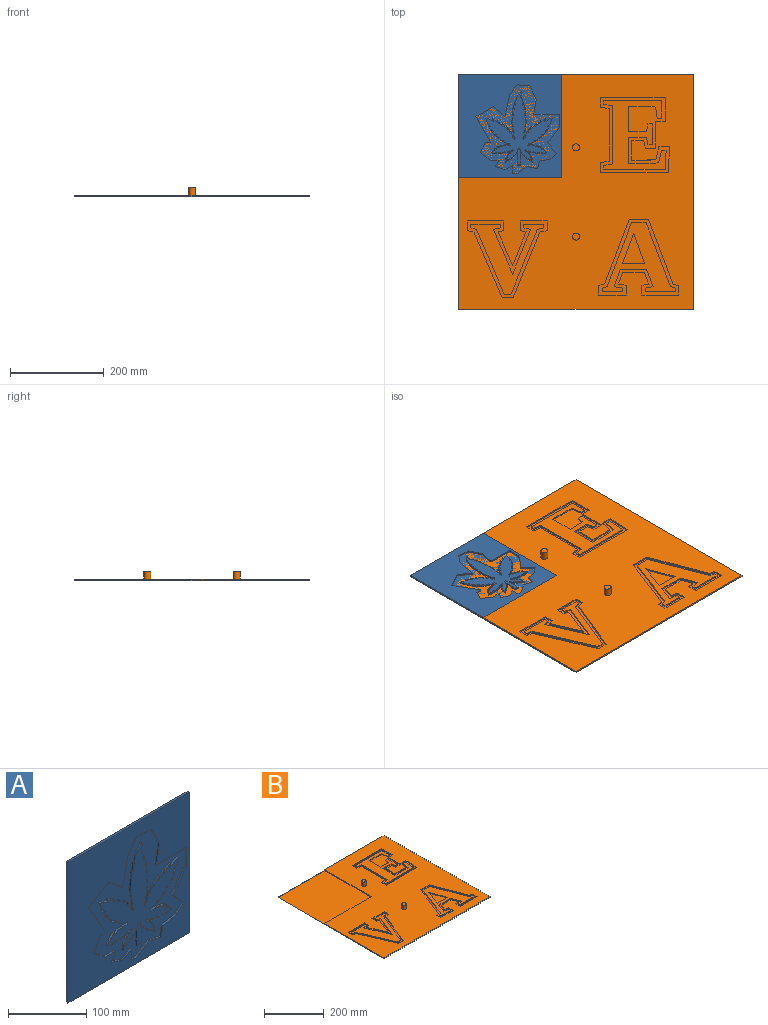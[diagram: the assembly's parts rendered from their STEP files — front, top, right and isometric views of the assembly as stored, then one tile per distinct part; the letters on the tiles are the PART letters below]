
ASSEMBLY  parts=2 mates=1
PART A: 206 faces, bbox 220x3.2x220 mm
  f0: plane 188.63x177.8mm, normal (0,-1,0), area 12442.7mm2, adj f1,f2,f3,f4,f5,f6,f7,f8
  f1: extruded ~4.79x3mm, area 15.3mm2, adj f0,f2,f127,f128
  f2: extruded ~10.54x3mm, area 31.8mm2, adj f0,f1,f3,f128
  f3: extruded ~3x2.61mm, area 9.2mm2, adj f0,f2,f128,f170
  f4: extruded ~8.42x4.29mm, area 28.5mm2, adj f0,f5,f128,f170
  f5: extruded ~6.25x3mm, area 18.9mm2, adj f0,f4,f6,f128
  f6: extruded ~14.48x5.45mm, area 46.6mm2, adj f0,f5,f128,f156
  f7: extruded ~15.1x6.7mm, area 50.4mm2, adj f0,f8,f128,f156
  f8: extruded ~5.75x3mm, area 17.4mm2, adj f0,f7,f9,f128
  f9: extruded ~11.4x6.85mm, area 40.5mm2, adj f0,f8,f128,f163
  f10: extruded ~12.15x8.66mm, area 45.4mm2, adj f0,f11,f128,f163
  f11: extruded ~4.86x3mm, area 14.7mm2, adj f0,f10,f12,f128
  f12: extruded ~10.68x10.21mm, area 44.6mm2, adj f0,f11,f128,f165
  f13: extruded ~18.78x10.4mm, area 65.3mm2, adj f0,f14,f128,f165
  f14: extruded ~16.33x6.61mm, area 53mm2, adj f0,f13,f15,f128
  f15: extruded ~5.23x3mm, area 17.7mm2, adj f0,f14,f128,f169
  f16: extruded ~5.42x3mm, area 18mm2, adj f0,f17,f128,f169
  f17: extruded ~11.43x11.4mm, area 48.6mm2, adj f0,f16,f18,f128
  f18: plane 6.01x3mm, normal (0.97,0,-0.25), area 18.6mm2, adj f0,f17,f19,f128
  f19: extruded ~13.14x10.95mm, area 51.4mm2, adj f0,f18,f128,f162
  f20: extruded ~11.99x6.68mm, area 41.5mm2, adj f0,f21,f128,f162
  f21: extruded ~6.27x3mm, area 18.9mm2, adj f0,f20,f22,f128
  f22: extruded ~17.17x5.92mm, area 54.6mm2, adj f0,f21,f128,f160
  f23: extruded ~6.86x3mm, area 21.8mm2, adj f0,f24,f128,f160
  f24: extruded ~4.75x3mm, area 14.8mm2, adj f0,f23,f25,f128
  f25: extruded ~3x2.73mm, area 9.8mm2, adj f0,f24,f128,f164
  f26: extruded ~4.25x3.31mm, area 16.3mm2, adj f0,f27,f128,f164
  f27: extruded ~15.58x4.44mm, area 48.8mm2, adj f0,f26,f28,f128
  f28: extruded ~3x2.1mm, area 9mm2, adj f0,f27,f128,f168
  f29: extruded ~17.07x3mm, area 51.8mm2, adj f0,f30,f128,f166
  f30: extruded ~3x2.68mm, area 10.7mm2, adj f0,f29,f31,f128
  f31: extruded ~16.02x3mm, area 48.5mm2, adj f0,f30,f128,f158
  f32: extruded ~13.69x3mm, area 41.7mm2, adj f0,f33,f128,f158
  f33: extruded ~4.72x3mm, area 15.7mm2, adj f0,f32,f34,f128
  f34: extruded ~16.76x3.75mm, area 52.3mm2, adj f0,f33,f128,f172
  f35: extruded ~12.57x9.28mm, area 47.2mm2, adj f0,f36,f128,f172
  f36: extruded ~16.76x3.75mm, area 52.3mm2, adj f0,f35,f37,f128
  f37: extruded ~4.72x3mm, area 15.7mm2, adj f0,f36,f128,f150
  f38: extruded ~3.47x3mm, area 13.6mm2, adj f0,f39,f128,f150
  f39: extruded ~16.02x3mm, area 48.5mm2, adj f0,f38,f40,f128
  f40: extruded ~3x2.68mm, area 10.7mm2, adj f0,f39,f128,f149
  f41: extruded ~13.2x3.25mm, area 41.3mm2, adj f0,f42,f128,f148
  f42: extruded ~3x2.1mm, area 9mm2, adj f0,f41,f43,f128
  f43: extruded ~15.58x4.44mm, area 48.8mm2, adj f0,f42,f128,f147
  f44: extruded ~14.36x5.59mm, area 46.8mm2, adj f0,f45,f128,f147
  f45: extruded ~3x2.73mm, area 9.8mm2, adj f0,f44,f46,f128
  f46: extruded ~4.75x3mm, area 14.8mm2, adj f0,f45,f128,f146
  f47: extruded ~3.87x3mm, area 11.9mm2, adj f0,f48,f128,f146
  f48: extruded ~17.17x5.92mm, area 54.6mm2, adj f0,f47,f49,f128
  f49: extruded ~6.27x3mm, area 18.9mm2, adj f0,f48,f128,f145
  f50: extruded ~13.14x10.95mm, area 51.4mm2, adj f0,f51,f128,f144
  f51: plane 6.01x3mm, normal (-0.97,0,-0.25), area 18.6mm2, adj f0,f50,f52,f128
  f52: extruded ~11.43x11.4mm, area 48.6mm2, adj f0,f51,f53,f128
  f53: extruded ~5.42x3mm, area 18mm2, adj f0,f52,f128,f143
  f54: extruded ~5.23x3mm, area 17.7mm2, adj f0,f55,f128,f143
  f55: extruded ~16.33x6.61mm, area 53mm2, adj f0,f54,f56,f128
  f56: extruded ~18.78x10.4mm, area 65.3mm2, adj f0,f55,f128,f142
  f57: extruded ~10.68x10.21mm, area 44.6mm2, adj f0,f58,f128,f142
  f58: extruded ~4.86x3mm, area 14.7mm2, adj f0,f57,f59,f128
  f59: extruded ~12.15x8.66mm, area 45.4mm2, adj f0,f58,f128,f141
  f60: extruded ~11.4x6.85mm, area 40.5mm2, adj f0,f61,f128,f141
  f61: extruded ~5.75x3mm, area 17.4mm2, adj f0,f60,f62,f128
  f62: extruded ~15.1x6.7mm, area 50.4mm2, adj f0,f61,f128,f140
  f63: extruded ~14.48x5.45mm, area 46.6mm2, adj f0,f64,f128,f140
  f64: extruded ~6.25x3mm, area 18.9mm2, adj f0,f63,f65,f128
  f65: extruded ~8.42x4.29mm, area 28.5mm2, adj f0,f64,f128,f139
  f66: extruded ~3x2.61mm, area 9.2mm2, adj f0,f67,f128,f139
  f67: extruded ~10.54x3mm, area 31.8mm2, adj f0,f66,f68,f128
  f68: extruded ~4.79x3mm, area 15.3mm2, adj f0,f67,f128,f138
  f69: extruded ~5.93x3mm, area 18.2mm2, adj f0,f70,f128,f138
  f70: extruded ~10.24x3.16mm, area 32.3mm2, adj f0,f69,f71,f128
  f71: extruded ~4.3x3mm, area 13.1mm2, adj f0,f70,f128,f137
  f72: extruded ~10.84x3mm, area 33mm2, adj f0,f73,f128,f137
  f73: extruded ~3.62x3mm, area 14.2mm2, adj f0,f72,f74,f128
  f74: extruded ~10.82x3mm, area 33.7mm2, adj f0,f73,f128,f136
  f75: extruded ~12.96x3.96mm, area 40.8mm2, adj f0,f76,f128,f136
  f76: extruded ~3.86x3mm, area 14.5mm2, adj f0,f75,f77,f128
  f77: extruded ~13.27x4.86mm, area 42.5mm2, adj f0,f76,f128,f135
  f78: extruded ~9.57x5.24mm, area 32.8mm2, adj f0,f79,f128,f135
  f79: extruded ~3x1.39mm, area 4.9mm2, adj f0,f78,f80,f128
  f80: extruded ~3x2.47mm, area 7.5mm2, adj f0,f79,f128,f134
  f81: extruded ~3x1.11mm, area 3.9mm2, adj f0,f82,f128,f134
  f82: extruded ~6.67x3.55mm, area 23mm2, adj f0,f81,f83,f128
  f83: extruded ~3x1.89mm, area 5.7mm2, adj f0,f82,f128,f133
  f84: extruded ~3x2.13mm, area 6.9mm2, adj f0,f85,f128,f133
  f85: extruded ~5.73x4.79mm, area 22.5mm2, adj f0,f84,f86,f128
  f86: extruded ~3x2.37mm, area 7.9mm2, adj f0,f85,f128,f132
  f87: extruded ~3x1.4mm, area 5mm2, adj f0,f88,f128,f132
  f88: extruded ~7.61x3mm, area 23.6mm2, adj f0,f87,f89,f128
  f89: extruded ~5.43x4.85mm, area 21.9mm2, adj f0,f88,f128,f131
  f90: extruded ~3.94x3.47mm, area 15.9mm2, adj f0,f91,f128,f131
  f91: extruded ~3x2.42mm, area 7.5mm2, adj f0,f90,f92,f128
  f92: extruded ~5.85x5.3mm, area 23.8mm2, adj f0,f91,f128,f130
  f93: extruded ~6.05x4.45mm, area 22.6mm2, adj f0,f94,f128,f130
  f94: extruded ~3.39x3mm, area 10.5mm2, adj f0,f93,f95,f128
  f95: extruded ~9.58x6.23mm, area 34.4mm2, adj f0,f94,f128,f129
  f96: extruded ~10.36x4.07mm, area 33.5mm2, adj f0,f97,f128,f129
  f97: extruded ~35.94x3mm, area 108.4mm2, adj f0,f96,f98,f128
  f98: extruded ~7.03x3mm, area 23.3mm2, adj f0,f97,f128,f171
  f99: extruded ~10.36x4.07mm, area 33.5mm2, adj f0,f100,f128,f171
  f100: extruded ~3x2.36mm, area 7.1mm2, adj f0,f99,f101,f128
  f101: extruded ~9.58x6.23mm, area 34.4mm2, adj f0,f100,f128,f159
  f102: extruded ~6.05x4.45mm, area 22.6mm2, adj f0,f103,f128,f159
  f103: extruded ~3x2.15mm, area 6.6mm2, adj f0,f102,f104,f128
  f104: extruded ~5.85x5.3mm, area 23.8mm2, adj f0,f103,f128,f154
  f105: extruded ~3.94x3.47mm, area 15.9mm2, adj f0,f106,f128,f154
  f106: extruded ~3x1.52mm, area 4.7mm2, adj f0,f105,f107,f128
  f107: extruded ~5.43x4.85mm, area 21.9mm2, adj f0,f106,f128,f167
  f108: extruded ~3x1.4mm, area 5mm2, adj f0,f109,f128,f167
  f109: extruded ~4.95x3.1mm, area 17.9mm2, adj f0,f108,f110,f128
  f110: extruded ~3x2.37mm, area 7.9mm2, adj f0,f109,f128,f151
  f111: extruded ~3x2.13mm, area 6.9mm2, adj f0,f112,f128,f151
  f112: extruded ~6.98x5.08mm, area 26.2mm2, adj f0,f111,f113,f128
  f113: extruded ~3x1.89mm, area 5.7mm2, adj f0,f112,f128,f153
  f114: extruded ~3x1.11mm, area 3.9mm2, adj f0,f115,f128,f153
  f115: extruded ~3x1.73mm, area 6.9mm2, adj f0,f114,f116,f128
  f116: extruded ~3x2.47mm, area 7.5mm2, adj f0,f115,f128,f152
  f117: extruded ~9.57x5.24mm, area 32.8mm2, adj f0,f118,f128,f152
  f118: extruded ~3x2.6mm, area 10.8mm2, adj f0,f117,f119,f128
  f119: extruded ~13.27x4.86mm, area 42.5mm2, adj f0,f118,f128,f157
  f120: extruded ~12.96x3.96mm, area 40.8mm2, adj f0,f121,f128,f157
  f121: extruded ~3.33x3mm, area 12.9mm2, adj f0,f120,f122,f128
  f122: extruded ~10.82x3mm, area 33.7mm2, adj f0,f121,f128,f155
  f123: extruded ~10.84x3mm, area 33mm2, adj f0,f124,f128,f155
  f124: extruded ~9.7x8.31mm, area 39mm2, adj f0,f123,f125,f128
  f125: extruded ~4.3x3mm, area 13.1mm2, adj f0,f124,f128,f161
  f126: extruded ~5.93x3mm, area 18.2mm2, adj f0,f127,f128,f161
  f127: extruded ~14.09x3mm, area 42.9mm2, adj f0,f1,f126,f128
  f128: plane 158.12x141.34mm, normal (0,-1,0), area 7762.5mm2, adj f1,f2,f3,f4,f5,f6,f7,f8
  f129: extruded ~3x2.36mm, area 7.1mm2, adj f0,f95,f96,f128
  f130: extruded ~3x2.15mm, area 6.6mm2, adj f0,f92,f93,f128
  f131: extruded ~3x1.52mm, area 4.7mm2, adj f0,f89,f90,f128
  f132: extruded ~4.95x3.1mm, area 17.9mm2, adj f0,f86,f87,f128
  f133: extruded ~6.98x5.08mm, area 26.2mm2, adj f0,f83,f84,f128
  f134: extruded ~3x1.73mm, area 6.9mm2, adj f0,f80,f81,f128
  f135: extruded ~3x2.6mm, area 10.8mm2, adj f0,f77,f78,f128
  f136: extruded ~3.33x3mm, area 12.9mm2, adj f0,f74,f75,f128
  f137: extruded ~9.7x8.31mm, area 39mm2, adj f0,f71,f72,f128
  f138: extruded ~14.09x3mm, area 42.9mm2, adj f0,f68,f69,f128
  f139: extruded ~12.14x3mm, area 36.7mm2, adj f0,f65,f66,f128
  f140: extruded ~3.91x3mm, area 12mm2, adj f0,f62,f63,f128
  f141: extruded ~4.42x3mm, area 13.5mm2, adj f0,f59,f60,f128
  f142: extruded ~5.35x3mm, area 17.2mm2, adj f0,f56,f57,f128
  f143: extruded ~13.22x9.99mm, area 49.8mm2, adj f0,f53,f54,f128
  f144: plane 5.72x3mm, normal (-0.98,0,-0.19), area 17.5mm2, adj f0,f50,f128,f145
  f145: extruded ~11.99x6.68mm, area 41.5mm2, adj f0,f49,f128,f144
  f146: extruded ~6.86x3mm, area 21.8mm2, adj f0,f46,f47,f128
  f147: extruded ~4.25x3.31mm, area 16.3mm2, adj f0,f43,f44,f128
  f148: plane 3.56x3mm, normal (0.81,0,0.58), area 13.1mm2, adj f0,f41,f128,f149
  f149: extruded ~17.07x3mm, area 51.8mm2, adj f0,f40,f128,f148
  f150: extruded ~13.69x3mm, area 41.7mm2, adj f0,f37,f38,f128
  f151: extruded ~5.73x4.79mm, area 22.5mm2, adj f0,f110,f111,f128
  f152: extruded ~3x1.39mm, area 4.9mm2, adj f0,f116,f117,f128
  f153: extruded ~6.67x3.55mm, area 23mm2, adj f0,f113,f114,f128
  f154: extruded ~3x2.42mm, area 7.5mm2, adj f0,f104,f105,f128
  f155: extruded ~3.62x3mm, area 14.2mm2, adj f0,f122,f123,f128
  f156: extruded ~3.91x3mm, area 12mm2, adj f0,f6,f7,f128
  f157: extruded ~3.86x3mm, area 14.5mm2, adj f0,f119,f120,f128
  f158: extruded ~3.47x3mm, area 13.6mm2, adj f0,f31,f32,f128
  f159: extruded ~3.39x3mm, area 10.5mm2, adj f0,f101,f102,f128
  f160: extruded ~3.87x3mm, area 11.9mm2, adj f0,f22,f23,f128
  f161: extruded ~10.24x3.16mm, area 32.3mm2, adj f0,f125,f126,f128
  f162: plane 5.72x3mm, normal (0.98,0,-0.19), area 17.5mm2, adj f0,f19,f20,f128
  f163: extruded ~4.42x3mm, area 13.5mm2, adj f0,f9,f10,f128
  f164: extruded ~14.36x5.59mm, area 46.8mm2, adj f0,f25,f26,f128
  f165: extruded ~5.35x3mm, area 17.2mm2, adj f0,f12,f13,f128
  f166: plane 3.56x3mm, normal (-0.81,0,0.58), area 13.1mm2, adj f0,f29,f128,f168
  f167: extruded ~7.61x3mm, area 23.6mm2, adj f0,f107,f108,f128
  f168: extruded ~13.2x3.25mm, area 41.3mm2, adj f0,f28,f128,f166
  f169: extruded ~13.22x9.99mm, area 49.8mm2, adj f0,f15,f16,f128
  f170: extruded ~12.14x3mm, area 36.7mm2, adj f0,f3,f4,f128
  f171: extruded ~35.94x3mm, area 108.4mm2, adj f0,f98,f99,f128
  f172: extruded ~12.57x3mm, area 38.4mm2, adj f0,f34,f35,f128
  f173: plane 24.87x20.34mm, normal (-0.63,0,-0.77), area 96.4mm2, adj f0,f174,f199,f200
  f174: plane 46.55x10.03mm, normal (0.98,0,-0.21), area 142.9mm2, adj f0,f173,f175,f200
  f175: plane 20.07x15.65mm, normal (0.79,0,-0.62), area 76.3mm2, adj f0,f174,f176,f200
  f176: plane 26.89x3mm, normal (-0.07,0,-1), area 80.9mm2, adj f0,f175,f177,f200
  f177: plane 28.89x14.05mm, normal (-0.9,0,-0.44), area 96.4mm2, adj f0,f176,f178,f200
  f178: plane 31.3x5.22mm, normal (-0.99,0,0.16), area 95.2mm2, adj f0,f177,f179,f200
  f179: plane 54.58x3mm, normal (0,0,-1), area 163.7mm2, adj f0,f178,f180,f200
  f180: plane 28.89x3mm, normal (-1,0,0), area 86.7mm2, adj f0,f179,f181,f200
  f181: plane 26.49x20.07mm, normal (-0.8,0,0.6), area 99.7mm2, adj f0,f180,f182,f200
  f182: plane 6.02x5.22mm, normal (-0.65,0,0.76), area 23.9mm2, adj f0,f181,f183,f200
  f183: plane 23.42x20.3mm, normal (-0.76,0,-0.65), area 93mm2, adj f0,f182,f184,f200
  f184: plane 14.68x12.3mm, normal (-0.64,0,0.77), area 57.4mm2, adj f0,f183,f185,f200
  f185: plane 22.47x4.01mm, normal (-0.18,0,0.98), area 68.5mm2, adj f0,f184,f186,f200
  f186: plane 16.45x3.61mm, normal (-0.98,0,0.21), area 50.5mm2, adj f0,f185,f187,f200
  f187: plane 22.28x4.89mm, normal (0.21,0,0.98), area 68.4mm2, adj f0,f186,f188,f200
  f188: plane 20.66x14.52mm, normal (-0.58,0,0.82), area 75.8mm2, adj f0,f187,f189,f200
  f189: plane 10.43x3mm, normal (0,0,1), area 31.3mm2, adj f0,f188,f190,f200
  f190: plane 16.45x3mm, normal (1,0,0), area 49.4mm2, adj f0,f189,f191,f200
  f191: plane 17.26x8.43mm, normal (-0.44,0,0.9), area 57.6mm2, adj f0,f190,f192,f200
  f192: plane 19.66x7.22mm, normal (0.34,0,0.94), area 62.8mm2, adj f0,f191,f193,f200
  f193: plane 13.24x8.43mm, normal (0.84,0,-0.54), area 47.1mm2, adj f0,f192,f194,f200
  f194: plane 18.86x3mm, normal (0,0,1), area 56.6mm2, adj f0,f193,f195,f200
  f195: plane 21.27x16.05mm, normal (0.6,0,0.8), area 79.9mm2, adj f0,f194,f196,f200
  f196: plane 21.27x10.84mm, normal (0.89,0,-0.45), area 71.6mm2, adj f0,f195,f197,f200
  f197: plane 11.64x3mm, normal (0,0,-1), area 34.9mm2, adj f0,f196,f198,f200
  f198: plane 55.38x31.7mm, normal (0.87,0,0.5), area 191.4mm2, adj f0,f197,f199,f200
  f199: plane 36.94x21.15mm, normal (0.5,0,-0.87), area 127.7mm2, adj f0,f173,f198,f200
  f200: plane 220x220mm, normal (0,-1,0), area 28194.8mm2, adj f173,f174,f175,f176,f177,f178,f179,f180
  f201: plane 220x220mm, normal (0,1,0), area 48400mm2, adj f202,f203,f204,f205
  f202: plane 220x3.2mm, normal (0,0,1), area 704mm2, adj f200,f201,f203,f205
  f203: plane 220x3.2mm, normal (1,0,0), area 704mm2, adj f200,f201,f202,f204
  f204: plane 220x3.2mm, normal (0,0,-1), area 704mm2, adj f200,f201,f203,f205
  f205: plane 220x3.2mm, normal (-1,0,0), area 704mm2, adj f200,f201,f202,f204
PART B: 130 faces, bbox 500x500x20.1 mm
  f0: plane 500x3.1mm, normal (0,1,0), area 890mm2, adj f73,f121,f122,f123,f128,f129
  f1: plane 170.67x160.7mm, normal (0,0,1), area 4787.6mm2, adj f4,f5,f6,f7,f8,f9,f10,f11
  f2: plane 64.34x23.96mm, normal (0.94,-0.35,0), area 206mm2, adj f3,f20,f21,f22
  f3: plane 64.34x23.33mm, normal (-0.94,-0.34,0), area 205.3mm2, adj f2,f20,f21,f22
  f4: plane 7.92x3mm, normal (1,0,0), area 23.7mm2, adj f1,f5,f19,f21
  f5: plane 18.68x3mm, normal (0.16,0.99,0), area 56.7mm2, adj f1,f4,f6,f21
  f6: plane 37.64x13.33mm, normal (0.94,-0.33,0), area 119.8mm2, adj f1,f5,f7,f21
  f7: plane 55.9x3mm, normal (0,-1,0), area 167.7mm2, adj f1,f6,f8,f21
  f8: plane 37.64x13.89mm, normal (-0.94,-0.35,0), area 120.4mm2, adj f1,f7,f9,f21
  f9: plane 16.84x3mm, normal (-0.17,0.98,0), area 51.3mm2, adj f1,f8,f10,f21
  f10: plane 7.92x3mm, normal (-1,0,0), area 23.7mm2, adj f1,f9,f11,f21
  f11: plane 64.79x3mm, normal (0,-1,0), area 194.4mm2, adj f1,f10,f12,f21
  f12: plane 7.92x3mm, normal (1,0,0), area 23.7mm2, adj f1,f11,f13,f21
  f13: plane 11.08x3mm, normal (0.26,0.97,0), area 34.4mm2, adj f1,f12,f14,f21
  f14: plane 135.83x51.53mm, normal (0.93,0.35,0), area 435.8mm2, adj f1,f13,f15,f21
  f15: plane 31.46x3mm, normal (0,1,0), area 94.4mm2, adj f1,f14,f16,f21
  f16: plane 135.83x51.77mm, normal (-0.93,0.36,0), area 436.1mm2, adj f1,f15,f17,f21
  f17: plane 10.83x3mm, normal (-0.26,0.96,0), area 33.7mm2, adj f1,f16,f18,f21
  f18: plane 7.92x3mm, normal (-1,0,0), area 23.7mm2, adj f1,f17,f19,f21
  f19: plane 44.27x3mm, normal (0,-1,0), area 132.8mm2, adj f1,f4,f18,f21
  f20: plane 47.29x3mm, normal (0,1,0), area 141.9mm2, adj f2,f3,f21,f22
  f21: plane 156.67x146.7mm, normal (0,0,1), area 8251.5mm2, adj f2,f3,f4,f5,f6,f7,f8,f9
  f22: plane 64.34x47.29mm, normal (0,0,1), area 1521.4mm2, adj f2,f3,f20
  f23: plane 20.9x3mm, normal (1,0,0), area 62.7mm2, adj f24,f70,f73,f120
  f24: plane 18.68x3mm, normal (0.16,-0.99,0), area 56.7mm2, adj f23,f25,f73,f120
  f25: plane 111.89x3mm, normal (1,0,0), area 335.7mm2, adj f24,f26,f73,f120
  f26: plane 18.68x3mm, normal (0.15,0.99,0), area 56.7mm2, adj f25,f27,f73,f120
  f27: plane 20.93x3mm, normal (1,0,0), area 62.8mm2, adj f26,f28,f73,f120
  f28: plane 137.92x3mm, normal (0,-1,0), area 413.8mm2, adj f27,f29,f73,f120
  f29: plane 51.01x3mm, normal (-1,0,0), area 153mm2, adj f28,f30,f73,f120
  f30: plane 19.97x3mm, normal (0,1,0), area 59.9mm2, adj f29,f31,f73,f120
  f31: plane 56.98x3mm, normal (-1,0,0), area 170.9mm2, adj f30,f32,f73,f120
  f32: plane 22.37x3mm, normal (0,1,0), area 67.1mm2, adj f31,f33,f73,f120
  f33: plane 16.49x3.37mm, normal (0.98,0.2,0), area 50.5mm2, adj f32,f34,f73,f120
  f34: plane 25.38x3mm, normal (0,1,0), area 76.1mm2, adj f33,f35,f73,f120
  f35: plane 42.08x3mm, normal (-1,0,0), area 126.2mm2, adj f34,f36,f73,f120
  f36: plane 20.47x3mm, normal (0,-1,0), area 61.4mm2, adj f35,f37,f73,f120
  f37: extruded ~30.92x3mm, area 92.8mm2, adj f36,f38,f73,f120
  f38: plane 27.65x6.35mm, normal (0.97,-0.22,0), area 85.1mm2, adj f37,f39,f73,f120
  f39: plane 22.84x3mm, normal (0,-1,0), area 68.5mm2, adj f38,f40,f73,f120
  f40: plane 54.59x3mm, normal (-1,0.05,0), area 164mm2, adj f39,f70,f73,f120
  f41: plane 16.27x3mm, normal (-0.16,-0.99,0), area 49.4mm2, adj f1,f42,f71,f73
  f42: plane 20.9x3mm, normal (-1,0,0), area 62.7mm2, adj f1,f41,f43,f73
  f43: plane 58.27x3mm, normal (0,1,0), area 174.8mm2, adj f1,f42,f44,f73
  f44: plane 20.26x3mm, normal (1,0,0), area 60.8mm2, adj f1,f43,f45,f73
  f45: plane 12.56x3.42mm, normal (0.26,-0.96,0), area 39.1mm2, adj f1,f44,f46,f73
  f46: plane 137.02x52.22mm, normal (0.93,-0.36,0), area 439.9mm2, adj f1,f45,f47,f73
  f47: plane 41.11x3mm, normal (0,-1,0), area 123.3mm2, adj f1,f46,f48,f73
  f48: plane 136.99x51.97mm, normal (-0.93,-0.35,0), area 439.6mm2, adj f1,f47,f49,f73
  f49: plane 12.81x3.41mm, normal (-0.26,-0.97,0), area 39.8mm2, adj f1,f48,f50,f73
  f50: plane 20.3x3mm, normal (-1,0,0), area 60.9mm2, adj f1,f49,f51,f73
  f51: plane 78.79x3mm, normal (0,1,0), area 236.4mm2, adj f1,f50,f52,f73
  f52: plane 20.8x3mm, normal (1,0,0), area 62.4mm2, adj f1,f51,f53,f73
  f53: plane 14.37x3mm, normal (0.17,-0.98,0), area 43.8mm2, adj f1,f52,f54,f73
  f54: plane 25.19x9.3mm, normal (0.94,0.35,0), area 80.6mm2, adj f1,f53,f55,f73
  f55: plane 46.08x3mm, normal (0,1,0), area 138.2mm2, adj f1,f54,f71,f73
  f56: plane 56.85x3mm, normal (0,-1,0), area 170.5mm2, adj f57,f72,f73,f92
  f57: plane 20.58x3mm, normal (-1,0,0), area 61.7mm2, adj f56,f58,f73,f92
  f58: plane 15.7x3.36mm, normal (-0.21,0.98,0), area 48.2mm2, adj f57,f59,f73,f92
  f59: plane 138.95x56.59mm, normal (-0.93,0.38,0), area 450.1mm2, adj f58,f60,f73,f92
  f60: plane 23.73x3mm, normal (0,1,0), area 71.2mm2, adj f59,f61,f73,f92
  f61: plane 139.06x59.58mm, normal (0.92,0.39,0), area 453.9mm2, adj f60,f62,f73,f92
  f62: plane 13.88x3.43mm, normal (0.24,0.97,0), area 42.9mm2, adj f61,f63,f73,f92
  f63: plane 20.4x3mm, normal (1,0,0), area 61.2mm2, adj f62,f64,f73,f92
  f64: plane 77.26x3mm, normal (0,-1,0), area 231.8mm2, adj f63,f65,f73,f92
  f65: plane 20.68x3mm, normal (-1,0,0), area 62mm2, adj f64,f66,f73,f92
  f66: plane 12.25x3mm, normal (-0.19,0.98,0), area 37.5mm2, adj f65,f67,f73,f92
  f67: plane 71.9x30.86mm, normal (-0.92,-0.39,0), area 234.7mm2, adj f66,f68,f73,f92
  f68: plane 71.91x28.8mm, normal (0.93,-0.37,0), area 232.4mm2, adj f67,f69,f73,f92
  f69: plane 12.03x3mm, normal (0.2,0.98,0), area 36.8mm2, adj f68,f72,f73,f92
  f70: plane 144.62x3mm, normal (0,1,0), area 433.9mm2, adj f23,f40,f73,f120
  f71: plane 25.04x8.87mm, normal (-0.94,0.33,0), area 79.7mm2, adj f1,f41,f55,f73
  f72: plane 20.65x3mm, normal (1,0,0), area 61.9mm2, adj f56,f69,f73,f92
  f73: plane 500x500mm, normal (0,0,1), area 156923.6mm2, adj f0,f23,f24,f25,f26,f27,f28,f29
  f74: plane 15x15mm, normal (0,0,1), area 176.7mm2, adj f75
  f75: cylinder r=7.5mm len=17mm, axis (0,0,-1), area 801.1mm2, adj f73,f74
  f76: plane 155.49x148.89mm, normal (0,0,1), area 7246.5mm2, adj f77,f78,f79,f80,f81,f82,f83,f84
  f77: plane 42.85x3mm, normal (0,1,0), area 128.5mm2, adj f76,f78,f91,f92
  f78: plane 7.92x3mm, normal (-1,0,0), area 23.8mm2, adj f76,f77,f79,f92
  f79: plane 14.65x3mm, normal (-0.2,-0.98,0), area 44.8mm2, adj f76,f78,f80,f92
  f80: plane 95.38x38.19mm, normal (-0.93,0.37,0), area 308.2mm2, adj f76,f79,f81,f92
  f81: plane 95.38x40.94mm, normal (0.92,0.39,0), area 311.4mm2, adj f76,f80,f82,f92
  f82: plane 15.1x3mm, normal (0.19,-0.98,0), area 46.2mm2, adj f76,f81,f83,f92
  f83: plane 7.92x3mm, normal (1,0,0), area 23.8mm2, adj f76,f82,f84,f92
  f84: plane 63.26x3mm, normal (0,1,0), area 189.8mm2, adj f76,f83,f85,f92
  f85: plane 7.92x3mm, normal (-1,0,0), area 23.8mm2, adj f76,f84,f86,f92
  f86: plane 11.94x3mm, normal (-0.24,-0.97,0), area 36.9mm2, adj f76,f85,f87,f92
  f87: plane 138.02x59.13mm, normal (-0.92,-0.39,0), area 450.5mm2, adj f76,f86,f88,f92
  f88: plane 14.41x3mm, normal (0,-1,0), area 43.2mm2, adj f76,f87,f89,f92
  f89: plane 138.02x56.22mm, normal (0.93,-0.38,0), area 447.1mm2, adj f76,f88,f90,f92
  f90: plane 13.78x3mm, normal (0.21,-0.98,0), area 42.3mm2, adj f76,f89,f91,f92
  f91: plane 7.92x3mm, normal (1,0,0), area 23.8mm2, adj f76,f77,f90,f92
  f92: plane 169.49x162.89mm, normal (0,0,1), area 5134.3mm2, adj f56,f57,f58,f59,f60,f61,f62,f63
  f93: plane 145.52x133.06mm, normal (0,0,1), area 8778.5mm2, adj f94,f95,f96,f97,f98,f99,f100,f101
  f94: plane 7.92x3mm, normal (-1,0,0), area 23.8mm2, adj f93,f95,f119,f120
  f95: plane 130.97x3mm, normal (0,-1,0), area 392.9mm2, adj f93,f94,f96,f120
  f96: plane 40.59x3mm, normal (1,-0.05,0), area 121.9mm2, adj f93,f95,f97,f120
  f97: plane 9.9x3mm, normal (0,1,0), area 29.7mm2, adj f93,f96,f98,f120
  f98: plane 26.91x6.18mm, normal (-0.97,0.22,0), area 82.8mm2, adj f93,f97,f99,f120
  f99: extruded ~36.67x3mm, area 110.2mm2, adj f93,f98,f100,f120
  f100: plane 27.47x3mm, normal (0,1,0), area 82.4mm2, adj f93,f99,f101,f120
  f101: plane 56.08x3mm, normal (1,0,0), area 168.2mm2, adj f93,f100,f102,f120
  f102: plane 38.09x3mm, normal (0,-1,0), area 114.3mm2, adj f93,f101,f103,f120
  f103: plane 16.49x3.37mm, normal (-0.98,-0.2,0), area 50.5mm2, adj f93,f102,f104,f120
  f104: plane 9.65x3mm, normal (0,-1,0), area 29mm2, adj f93,f103,f105,f120
  f105: plane 44.72x3mm, normal (1,0,0), area 134.2mm2, adj f93,f104,f106,f120
  f106: plane 9.65x3mm, normal (0,1,0), area 29mm2, adj f93,f105,f107,f120
  f107: plane 16.08x3.37mm, normal (-0.98,0.21,0), area 49.3mm2, adj f93,f106,f108,f120
  f108: plane 38.09x3mm, normal (0,1,0), area 114.3mm2, adj f93,f107,f109,f120
  f109: plane 53.4x3mm, normal (1,0,0), area 160.2mm2, adj f93,f108,f110,f120
  f110: plane 22.57x3mm, normal (0,-1,0), area 67.7mm2, adj f93,f109,f111,f120
  f111: extruded ~35.17x3mm, area 105.7mm2, adj f93,f110,f112,f120
  f112: plane 23.54x3.47mm, normal (-0.99,-0.15,0), area 71.4mm2, adj f93,f111,f113,f120
  f113: plane 9.86x3mm, normal (0,-1,0), area 29.6mm2, adj f93,f112,f114,f120
  f114: plane 37.01x3mm, normal (1,0,0), area 111mm2, adj f93,f113,f115,f120
  f115: plane 123.92x3mm, normal (0,1,0), area 371.8mm2, adj f93,f114,f116,f120
  f116: plane 7.92x3mm, normal (-1,0,0), area 23.7mm2, adj f93,f115,f117,f120
  f117: plane 18.68x3mm, normal (-0.15,-0.99,0), area 56.7mm2, adj f93,f116,f118,f120
  f118: plane 123.89x3mm, normal (-1,0,0), area 371.7mm2, adj f93,f117,f119,f120
  f119: plane 18.68x3mm, normal (-0.16,0.99,0), area 56.7mm2, adj f93,f94,f118,f120
  f120: plane 159.52x147.42mm, normal (0,0,1), area 8603.2mm2, adj f23,f24,f25,f26,f27,f28,f29,f30
  f121: plane 500x500mm, normal (0,0,-1), area 250000mm2, adj f0,f122,f123,f124
  f122: plane 500x3.1mm, normal (-1,0,0), area 890mm2, adj f0,f73,f121,f124,f127,f129
  f123: plane 500x3.1mm, normal (1,0,0), area 1550mm2, adj f0,f73,f121,f124
  f124: plane 500x3.1mm, normal (0,-1,0), area 1550mm2, adj f73,f121,f122,f123
  f125: plane 15x15mm, normal (0,0,1), area 176.7mm2, adj f126
  f126: cylinder r=7.5mm len=17mm, axis (0,0,-1), area 801.1mm2, adj f73,f125
  f127: plane 220x3mm, normal (0,1,0), area 660mm2, adj f73,f122,f128,f129
  f128: plane 220x3mm, normal (-1,0,0), area 660mm2, adj f0,f73,f127,f129
  f129: plane 220x220mm, normal (0,0,1), area 48400mm2, adj f0,f122,f127,f128
PLACE A rot(axis=(-1,0,0),90deg) t=(-120.25,119.41,-10.61)mm
PLACE B t=(-0.25,-0.59,-10.61)mm
MATE fastened A.f0 <-> B.f129  axis (0,0,1) through (-122.14,128.09,-10.61)mm
